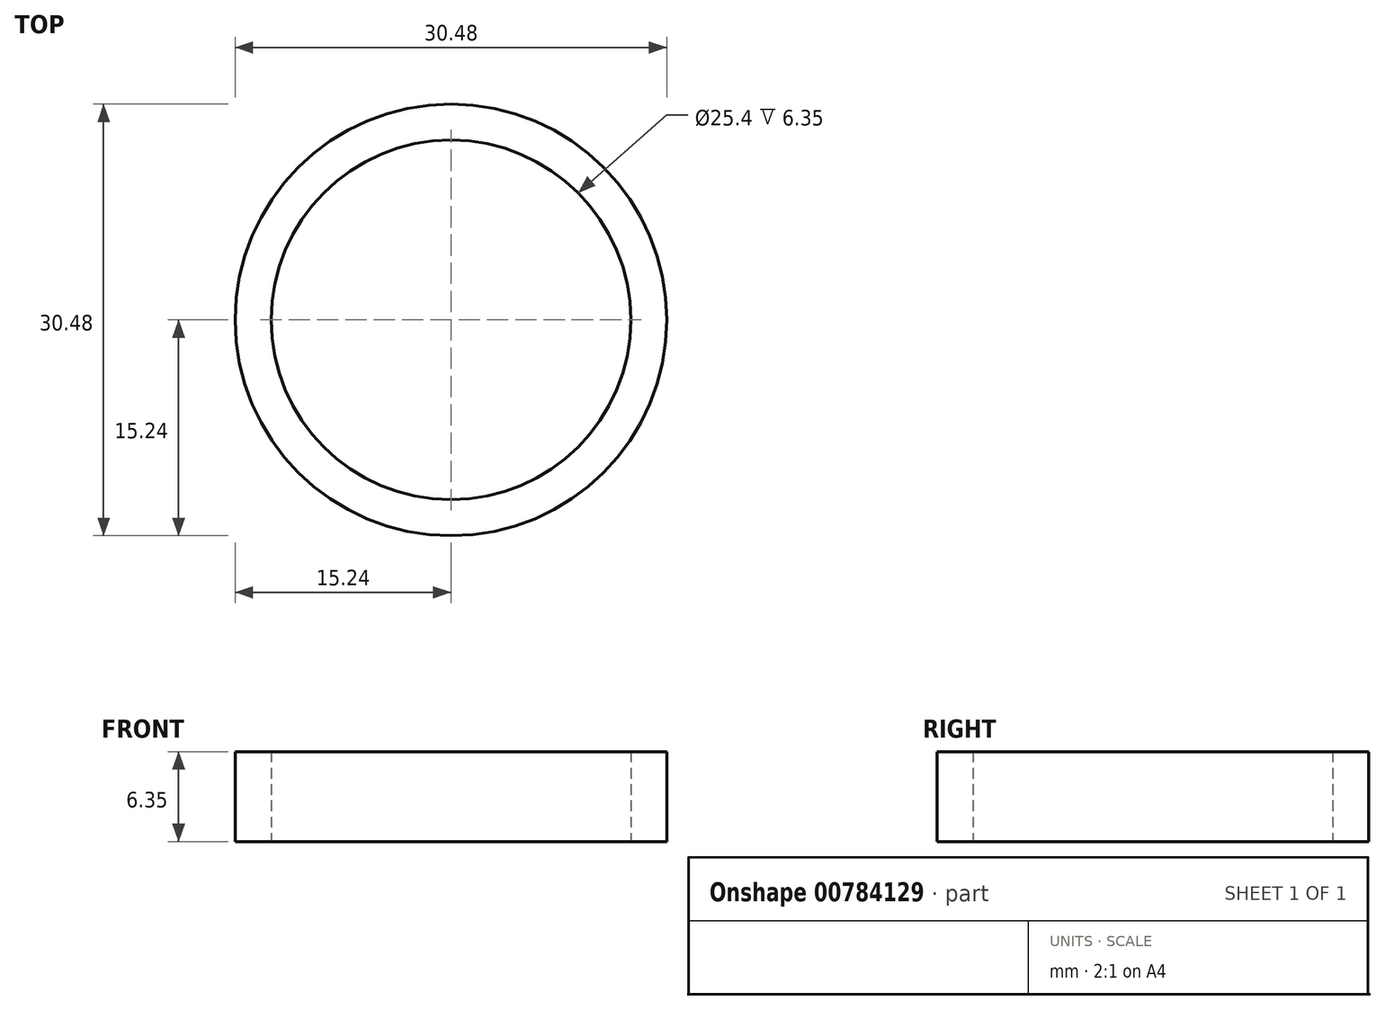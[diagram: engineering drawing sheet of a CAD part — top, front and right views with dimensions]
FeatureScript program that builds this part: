
annotation { "Feature Type Name" : "Feature", "Feature Type Description" : "" }
export const myFeature = defineFeature(function(context is Context, id is Id, definition is map)
    precondition{}
    {
        {
            var Q0;
            Q0=qCreatedBy(makeId("Top.planeOp"),FACE);
            var sketch = newSketch(context, id + "F0", { "sketchPlane" : qUnion([Q0])});
            skCircle(sketch, "E0", {"center": v(0, 0) * mm, "radius": 12.7 * mm});
            skCircle(sketch, "E1", {"center": v(0, 0) * mm, "radius": 15.24 * mm});
            skSolve(sketch);
        }
        {
            var Q0;
            Q0=makeQuery(id+"F0.imprint","IMPRINT",FACE,{"disambiguationData":[TD([[makeQuery(id+"F0.imprint","IMPRINT",EDGE,{"derivedFrom":sQuery(id+"F0.wireOp",EDGE,"E0")}),-1.0]])]});
            extrude(context, id + "F1", {"entities" : qUnion([Q0]), "depth" : 6.35 * mm, "offsetDistance" : 25.4 * mm});
        }
    });
